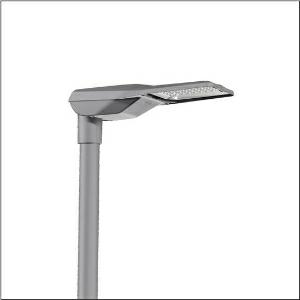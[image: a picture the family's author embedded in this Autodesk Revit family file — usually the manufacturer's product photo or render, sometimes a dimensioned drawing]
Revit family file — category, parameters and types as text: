
# Revit family: streetlight_sl_21_iq_mini___st1_0a_5xe2d31g08jb_707a
name_source: partatom
category: Lighting Fixtures
units: mm (PartAtom-declared; Revit-internal decimal feet)

## family parameters
Cut with Voids When Loaded = No
Host = Face
Light Source = No
Part Type = Normal
Room Calculation Point = No
Round Connector Dimension = Use Diameter
Shared = No

## types (1)
- --- (1 x LED, 10820 lm, 71.6 W, 3000K)
    Apparent Load = 72 VA
    CIE Flux Codes = 40 73 97 100 100
    Color Rendering = 70
    Color Temperature = 3000K
    Default Elevation = 1800 mm
    Description = Streetlight SL 21 mini, mast luminaire, primary light control with lens, of PMMA, primary optical cover: cover, of toughened safety glass, transparent, light distribution: ST1.0a, light emission: direct distribution, primary light characteristic: asymmetric, installation type: post-top, side-entry, LED, High Power LED, rated luminous flux: 10.820lm, luminous efficacy: 151lm/W, light colour: 730, colour temperature: 3000K, control gear: ECG iQ, control: Street-Remote, Auto-Match, Temp-Guard, Lumen-Switch, Night-Set, Smart-Wire, Light-Fading, Desk-Remote (wireless, voltage-free reading and setting of iQ features in the workshop via application-optimized NFC function/RFID function), optimised constant luminous flux control (CLO 2.0), mains connection: 220..240V, AC, 50/60Hz, start of lifetime: 72W, end of lifetime: 75W, reduction: 33W, luminaire housing, of diecast aluminium, powder-coated, Siteco® metallic grey (DB 702S), corrosivity category C5 according to DIN EN ISO 12944, length: 628mm, width: 235mm, height: 110mm, spigot size: 60/76mm (post-top) and 42/60/76mm (side-entry), mast flange for spigot size: 42mm: 5XC10008XM4, 60mm: 5XC10008XM2, 76/60mm: 5XC10108XM1, protection rating (complete): IP66, insulation class (complete): insulation class II (safety insulation), certification: CE, ENEC, VDE, impact resistance: IK09, permissible operating ambient temperature for outdoor applications: -40..+50°C, standard-compliant lighting for roads and squares, packaging unit: 1 piece

Light Distribution: ST1.0a
    Height = 110 mm
    Lamp = 1 x LED
    Lamp Light Flux = 10820 lm
    Lamp Power = 71.6 W
    Lamp count = 1
    Length = 625 mm
    Luminous efficacy = 151 lm/W
    Manufacturer = Siteco
    ModVariant = No
    Model = 5XE2D31G08JB
    Number of Poles = 1
    OnlyDefault = Yes
    Power Factor = 1
    Product Name = Streetlight SL 21 iQ mini | ST1.0a
    Product group = mast luminaire | pylon top
    ProductGroupID = 6100
    Protection Class = Protection class II
    Protection Degree = IP 66
    RLX_Detail_Level = 1
    RlxData = <blob elided: 93713 chars, md5=1490f96d>
    Socket = socket
    Standby Power = 0 W
    System Light Flux = 10820 lm
    System Power = 72 W
    Type Comments = factory setting: luminous flux: 100 % | dim-lin: 254 | 746 mA
    Type Image = l_1003519.jpg
    URL = http://relux.com
    VarID = @adj_083251
    Voltage = 0 V
    Weight = 0.00 kg
    Width = 234 mm

## geometry (parser evidence)
native form markers: Blend x4, Sweep x9
no freeform markers — native parametric forms only
